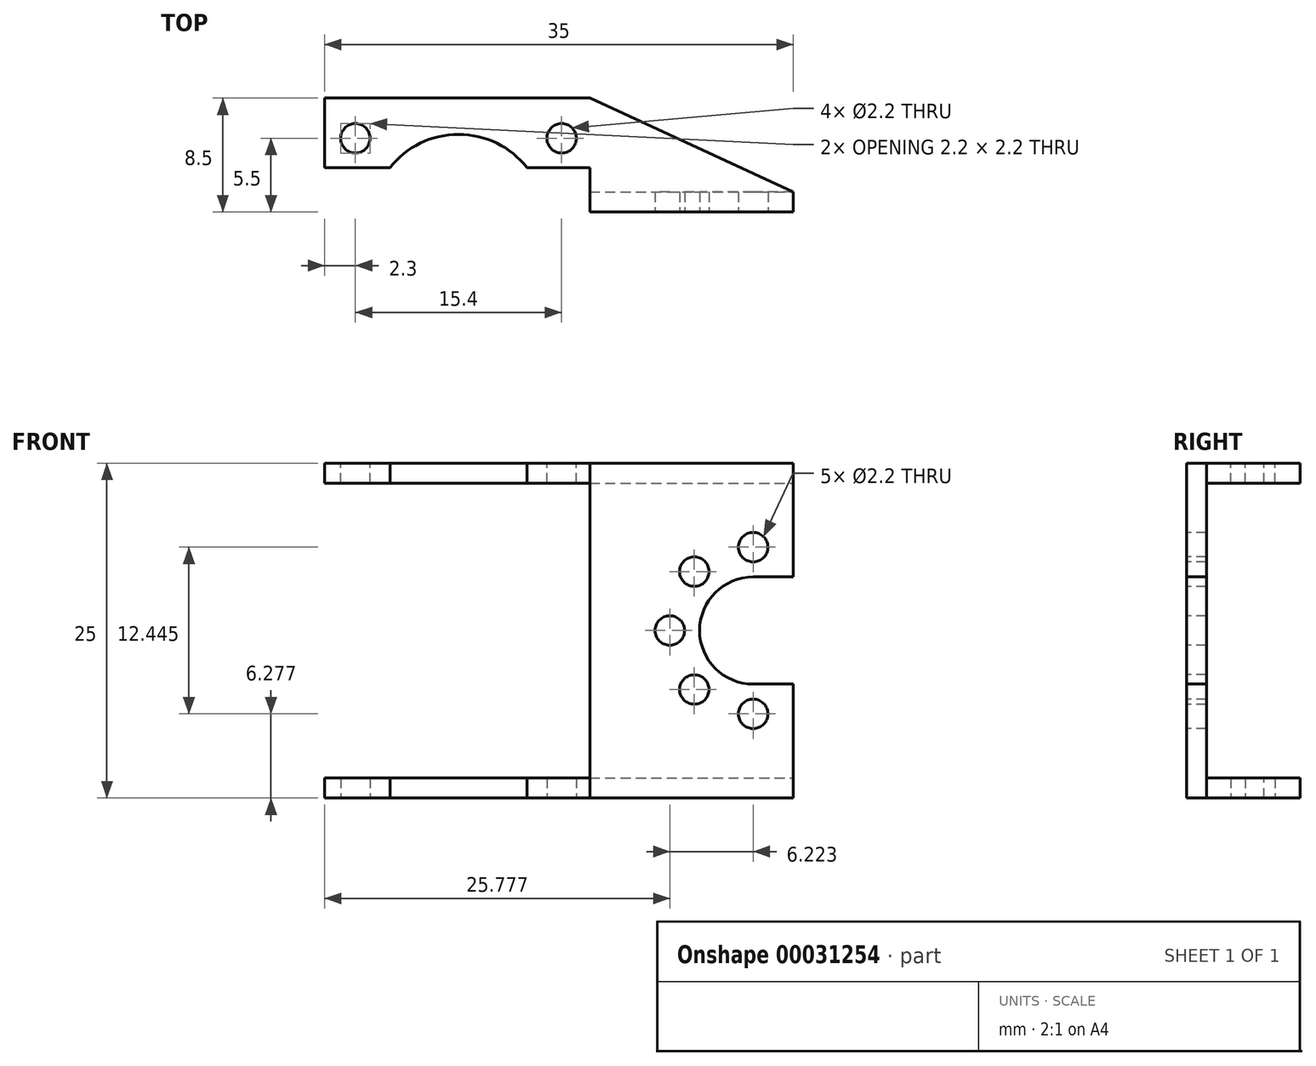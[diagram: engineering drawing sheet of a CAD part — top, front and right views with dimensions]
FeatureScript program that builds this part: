
annotation { "Feature Type Name" : "Feature", "Feature Type Description" : "" }
export const myFeature = defineFeature(function(context is Context, id is Id, definition is map)
    precondition{}
    {
        {
            var Q0;
            Q0=qCreatedBy(makeId("Top.planeOp"),FACE);
            var sketch = newSketch(context, id + "F0", { "sketchPlane" : qUnion([Q0])});
            skLineSegment(sketch, "E0.bottom", {"start": v(-10, 0.75) * mm, "end": v(10, 0.75) * mm});
            skLineSegment(sketch, "E0.top", {"start": v(-10, -0.75) * mm, "end": v(10, -0.75) * mm});
            skLineSegment(sketch, "E0.left", {"start": v(-10, 0.75) * mm, "end": v(-10, -0.75) * mm});
            skLineSegment(sketch, "E0.right", {"start": v(10, 0.75) * mm, "end": v(10, -0.75) * mm});
            skPoint(sketch, "E0.middle", {"position": v(0, 0) * mm});
            skSolve(sketch);
        }
        {
            var Q0;
            Q0 = qSketchRegion(id + "F0", true);
            extrude(context, id + "F1", {"entities" : qUnion([Q0]), "depth" : (11 + 1.5) * mm});
        }
        {
            var Q0;
            Q0=makeQuery(id+"F1.opExtrude","SWEPT_FACE",FACE,{"disambiguationData":[OSD([sQuery(id+"F0.wireOp",EDGE,"E0.bottom")])]});
            var sketch = newSketch(context, id + "F2", { "sketchPlane" : qUnion([Q0])});
            skLineSegment(sketch, "E1.bottom", {"start": v(10, 12.5) * mm, "end": v(-10, 12.5) * mm});
            skLineSegment(sketch, "E1.top", {"start": v(10, 11) * mm, "end": v(-10, 11) * mm});
            skLineSegment(sketch, "E1.left", {"start": v(10, 12.5) * mm, "end": v(10, 11) * mm});
            skLineSegment(sketch, "E1.right", {"start": v(-10, 12.5) * mm, "end": v(-10, 11) * mm});
            skSolve(sketch);
        }
        {
            var Q0;
            Q0 = qSketchRegion(id + "F2", true);
            extrude(context, id + "F3", {"entities" : qUnion([Q0]), "operationType" : NewBodyOperationType.ADD, "depth" : (10 - 1.5) * mm});
        }
        {
            var Q0;
            Q0=makeQuery(id+"F3.boolean.opBoolean","MERGE",FACE,{"derivedFrom":[makeQuery(id+"F1.opExtrude","CAP_FACE",FACE,{"disambiguationData":[OSD([sQuery(id+"F0.wireOp",EDGE,"E0.bottom"),sQuery(id+"F0.wireOp",EDGE,"E0.top"),sQuery(id+"F0.wireOp",EDGE,"E0.left"),sQuery(id+"F0.wireOp",EDGE,"E0.right")])],"isStart":false}),makeQuery(id+"F3.opExtrude","SWEPT_FACE",FACE,{"disambiguationData":[OSD([sQuery(id+"F2.wireOp",EDGE,"E1.bottom")])]})]});
            var sketch = newSketch(context, id + "F4", { "sketchPlane" : qUnion([Q0])});
            skLineSegment(sketch, "E2", {"start": v(-10, 4.75) * mm, "end": v(10, 4.75) * mm, "construction": true});
            skCircle(sketch, "E3", {"center": v(-7.7, 4.75) * mm, "radius": 1.1 * mm});
            skCircle(sketch, "E4.MirrorC", {"center": v(7.7, 4.75) * mm, "radius": 1.1 * mm});
            skSolve(sketch);
        }
        {
            var Q0;
            Q0 = qSketchRegion(id + "F4", true);
            extrude(context, id + "F5", {"entities" : qUnion([Q0]), "operationType" : NewBodyOperationType.REMOVE, "endBound" : BoundingType.UP_TO_NEXT, "oppositeDirection" : true, "depth" : 25 * mm});
        }
        {
            var Q0;
            Q0=makeQuery(id+"F1.opExtrude","SWEPT_BODY",BODY,{"disambiguationData":[OSD([sQuery(id+"F0.wireOp",EDGE,"E0.bottom"),sQuery(id+"F0.wireOp",EDGE,"E0.top"),sQuery(id+"F0.wireOp",EDGE,"E0.left"),sQuery(id+"F0.wireOp",EDGE,"E0.right")])]});
            var Q1;
            Q1=qCreatedBy(makeId("Top.planeOp"),FACE);
            mirror(context, id + "F6", {"operationType" : NewBodyOperationType.ADD, "entities" : qUnion([Q0]), "mirrorPlane" : qUnion([Q1])});
        }
        {
            var Q0;
            {var subQ0=makeQuery(id+"F3.boolean.opBoolean","MERGE",FACE,{"derivedFrom":[makeQuery(id+"F1.opExtrude","SWEPT_FACE",FACE,{"disambiguationData":[OSD([sQuery(id+"F0.wireOp",EDGE,"E0.right")])]}),makeQuery(id+"F3.opExtrude","SWEPT_FACE",FACE,{"disambiguationData":[OSD([sQuery(id+"F2.wireOp",EDGE,"E1.right")])]})]});Q0=makeQuery(id+"F6.boolean.opBoolean","MERGE",FACE,{"derivedFrom":[subQ0,makeQuery(id+"F6.opPattern","COPY",FACE,{"derivedFrom":subQ0,"instanceName":"1"})]});}
            var sketch = newSketch(context, id + "F7", { "sketchPlane" : qUnion([Q0])});
            skLineSegment(sketch, "E5.0", {"start": v(9.25, -12.5) * mm, "end": v(-0.75, -12.5) * mm});
            skLineSegment(sketch, "E5.1", {"start": v(9.25, 11) * mm, "end": v(0.75, 11) * mm});
            skLineSegment(sketch, "E5.2", {"start": v(9.25, -11) * mm, "end": v(0.75, -11) * mm});
            skLineSegment(sketch, "E5.3", {"start": v(9.25, 12.5) * mm, "end": v(-0.75, 12.5) * mm});
            skLineSegment(sketch, "E5.4", {"start": v(9.25, 11) * mm, "end": v(0.75, 11) * mm});
            skLineSegment(sketch, "E5.5", {"start": v(5.85, 12.5) * mm, "end": v(3.65, 12.5) * mm});
            skLineSegment(sketch, "E5.7", {"start": v(9.25, -12.5) * mm, "end": v(-0.75, -12.5) * mm});
            skLineSegment(sketch, "E5.8", {"start": v(9.25, -12.5) * mm, "end": v(9.25, -11) * mm});
            skLineSegment(sketch, "E5.9", {"start": v(9.25, 12.5) * mm, "end": v(9.25, 11) * mm});
            skLineSegment(sketch, "E5.10", {"start": v(9.25, 12.5) * mm, "end": v(-0.75, 12.5) * mm});
            skLineSegment(sketch, "E5.13", {"start": v(9.25, -11) * mm, "end": v(0.75, -11) * mm});
            skLineSegment(sketch, "E5.14", {"start": v(0.75, 11) * mm, "end": v(0.75, -11) * mm});
            skLineSegment(sketch, "E5.15", {"start": v(-0.75, 12.5) * mm, "end": v(-0.75, -12.5) * mm});
            skLineSegment(sketch, "E5.16", {"start": v(5.85, -11) * mm, "end": v(3.65, -11) * mm});
            skLineSegment(sketch, "E5.20", {"start": v(5.85, 11) * mm, "end": v(3.65, 11) * mm});
            skLineSegment(sketch, "E5.21", {"start": v(3.65, -11) * mm, "end": v(5.85, -11) * mm});
            skLineSegment(sketch, "E5.22", {"start": v(-0.75, 12.5) * mm, "end": v(-0.75, -12.5) * mm});
            skLineSegment(sketch, "E5.23", {"start": v(5.85, -12.5) * mm, "end": v(3.65, -12.5) * mm});
            skLineSegment(sketch, "E5.24", {"start": v(0.75, 11) * mm, "end": v(0.75, -11) * mm});
            skLineSegment(sketch, "E5.26", {"start": v(3.65, 12.5) * mm, "end": v(5.85, 12.5) * mm});
            skLineSegment(sketch, "E5.28", {"start": v(9.25, -12.5) * mm, "end": v(9.25, -11) * mm});
            skLineSegment(sketch, "E5.29", {"start": v(3.65, -12.5) * mm, "end": v(5.85, -12.5) * mm});
            skLineSegment(sketch, "E5.30", {"start": v(9.25, 12.5) * mm, "end": v(9.25, 11) * mm});
            skLineSegment(sketch, "E5.31", {"start": v(3.65, 11) * mm, "end": v(5.85, 11) * mm});
            skSolve(sketch);
        }
        {
            var Q0;
            Q0 = qSketchRegion(id + "F7", true);
            extrude(context, id + "F8", {"entities" : qUnion([Q0]), "operationType" : NewBodyOperationType.ADD, "depth" : 15 * mm});
        }
        {
            var Q0;
            {var subQ0=makeQuery(id+"F1.opExtrude","SWEPT_FACE",FACE,{"disambiguationData":[OSD([sQuery(id+"F0.wireOp",EDGE,"E0.top")])]});Q0=makeQuery(id+"F8.boolean.opBoolean","MERGE",FACE,{"derivedFrom":[makeQuery(id+"F6.boolean.opBoolean","MERGE",FACE,{"derivedFrom":[subQ0,makeQuery(id+"F6.opPattern","COPY",FACE,{"derivedFrom":subQ0,"instanceName":"1"})]}),makeQuery(id+"F8.opExtrude","SWEPT_FACE",FACE,{"disambiguationData":[OSD([sQuery(id+"F7.wireOp",EDGE,"E5.22")])]})]});}
            var sketch = newSketch(context, id + "F9", { "sketchPlane" : qUnion([Q0])});
            skArc(sketch, "E6", {"start": v(22, 4) * mm, "mid": v(18, 0) * mm, "end": v(22, -4) * mm});
            skLineSegment(sketch, "E7.bottom", {"start": v(17.6, -4.4) * mm, "end": v(26.4, -4.4) * mm, "construction": true});
            skLineSegment(sketch, "E7.top", {"start": v(17.6, 4.4) * mm, "end": v(26.4, 4.4) * mm, "construction": true});
            skLineSegment(sketch, "E7.left", {"start": v(17.6, -4.4) * mm, "end": v(17.6, 4.4) * mm, "construction": true});
            skLineSegment(sketch, "E7.right", {"start": v(26.4, -4.4) * mm, "end": v(26.4, 4.4) * mm, "construction": true});
            skCircle(sketch, "E8", {"center": v(17.6, -4.4) * mm, "radius": 1.1 * mm});
            skCircle(sketch, "E9.1.0", {"center": v(22, -6.22) * mm, "radius": 1.1 * mm});
            skCircle(sketch, "E9.5.0", {"center": v(22, 6.22) * mm, "radius": 1.1 * mm});
            skCircle(sketch, "E9.6.0", {"center": v(17.6, 4.4) * mm, "radius": 1.1 * mm});
            skCircle(sketch, "E9.7.0", {"center": v(15.78, 0) * mm, "radius": 1.1 * mm});
            skLineSegment(sketch, "E10", {"start": v(22, -4) * mm, "end": v(25, -4) * mm});
            skLineSegment(sketch, "E11", {"start": v(22, 4) * mm, "end": v(25, 4) * mm});
            skLineSegment(sketch, "E12", {"start": v(25, -4) * mm, "end": v(25, 4) * mm});
            skLineSegment(sketch, "E13.bottom", {"start": v(-10, -12.5) * mm, "end": v(9.8, -12.5) * mm});
            skLineSegment(sketch, "E13.top", {"start": v(-10, 12.5) * mm, "end": v(9.8, 12.5) * mm});
            skLineSegment(sketch, "E13.left", {"start": v(-10, -12.5) * mm, "end": v(-10, 12.5) * mm});
            skLineSegment(sketch, "E13.right", {"start": v(9.8, -12.5) * mm, "end": v(9.8, 12.5) * mm});
            skSolve(sketch);
        }
        {
            var Q0;
            Q0 = qSketchRegion(id + "F9", true);
            extrude(context, id + "F10", {"entities" : qUnion([Q0]), "operationType" : NewBodyOperationType.REMOVE, "oppositeDirection" : true, "depth" : 3.3 * mm});
        }
        {
            var Q0;
            Q0=makeQuery(id+"F8.boolean.opBoolean","MERGE",FACE,{"derivedFrom":[makeQuery(id+"F3.boolean.opBoolean","MERGE",FACE,{"derivedFrom":[makeQuery(id+"F1.opExtrude","CAP_FACE",FACE,{"disambiguationData":[OSD([sQuery(id+"F0.wireOp",EDGE,"E0.bottom"),sQuery(id+"F0.wireOp",EDGE,"E0.top"),sQuery(id+"F0.wireOp",EDGE,"E0.left"),sQuery(id+"F0.wireOp",EDGE,"E0.right")])],"isStart":false}),makeQuery(id+"F3.opExtrude","SWEPT_FACE",FACE,{"disambiguationData":[OSD([sQuery(id+"F2.wireOp",EDGE,"E1.bottom")])]})]}),makeQuery(id+"F8.opExtrude","SWEPT_FACE",FACE,{"disambiguationData":[OSD([sQuery(id+"F7.wireOp",EDGE,"E5.10"),sQuery(id+"F7.wireOp",EDGE,"E5.26")])]})]});
            var sketch = newSketch(context, id + "F11", { "sketchPlane" : qUnion([Q0])});
            skArc(sketch, "E14", {"start": v(5.12, 2.55) * mm, "mid": v(0, 5.05) * mm, "end": v(-5.12, 2.55) * mm});
            skPoint(sketch, "E15", {"position": v(-7.7, 4.75) * mm});
            skPoint(sketch, "E16", {"position": v(7.7, 4.75) * mm});
            skLineSegment(sketch, "E17", {"start": v(-7.7, 4.75) * mm, "end": v(7.7, 4.75) * mm, "construction": true});
            skPoint(sketch, "E18", {"position": v(0, 4.75) * mm});
            skLineSegment(sketch, "E19", {"start": v(-5.12, 2.55) * mm, "end": v(5.12, 2.55) * mm});
            skLineSegment(sketch, "E20", {"start": v(-10, 7.75) * mm, "end": v(9.8, 7.75) * mm});
            skLineSegment(sketch, "E21", {"start": v(9.8, 7.75) * mm, "end": v(25, 0.75) * mm});
            skLineSegment(sketch, "E22", {"start": v(-10, 7.55) * mm, "end": v(9.8, 7.55) * mm, "construction": true});
            skLineSegment(sketch, "E23", {"start": v(9.8, 7.75) * mm, "end": v(9.8, 7.55) * mm, "construction": true});
            skSolve(sketch);
        }
        {
            var Q0;
            Q0 = qSketchRegion(id + "F11", true);
            var Q1;
            {var subQ5=sQuery(id+"F11.wireOp",EDGE,"E20");Q1=makeQuery(id+"F11.imprint","IMPRINT",FACE,{"disambiguationData":[TD([[makeQuery(id+"F11.imprint","IMPRINT",EDGE,{"derivedFrom":subQ5}),1.0]])]});}
            var Q2;
            {var subQ4=sQuery(id+"F11.wireOp",EDGE,"E21");Q2=makeQuery(id+"F11.imprint","IMPRINT",FACE,{"disambiguationData":[TD([[makeQuery(id+"F11.imprint","IMPRINT",EDGE,{"derivedFrom":subQ4}),1.0]])]});}
            extrude(context, id + "F12", {"entities" : qUnion([Q0, Q1, Q2]), "operationType" : NewBodyOperationType.REMOVE, "endBound" : BoundingType.THROUGH_ALL, "oppositeDirection" : true, "depth" : 25 * mm});
        }
    });
